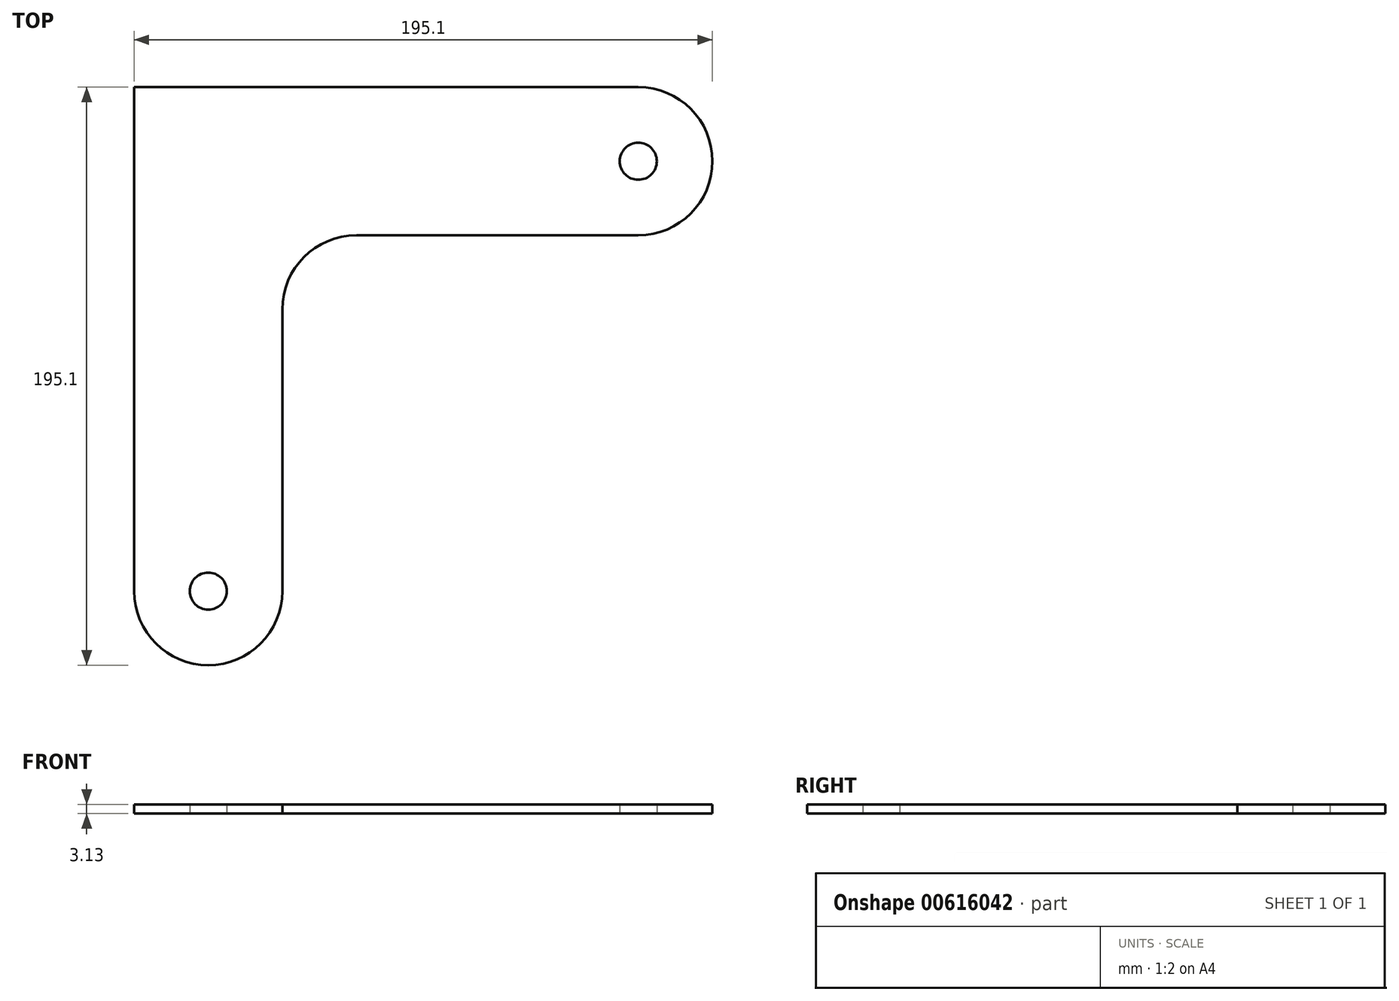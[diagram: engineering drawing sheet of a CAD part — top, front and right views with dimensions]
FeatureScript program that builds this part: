
annotation { "Feature Type Name" : "Feature", "Feature Type Description" : "" }
export const myFeature = defineFeature(function(context is Context, id is Id, definition is map)
    precondition{}
    {
        {
            var Q0;
            Q0=qCreatedBy(makeId("Top.planeOp"),FACE);
            var sketch = newSketch(context, id + "F0", { "sketchPlane" : qUnion([Q0])});
            skLineSegment(sketch, "E0", {"start": v(170.1, 0) * mm, "end": v(0, 0) * mm});
            skLineSegment(sketch, "E1", {"start": v(0, 0) * mm, "end": v(0, -170.1) * mm});
            skLineSegment(sketch, "E2", {"start": v(50, -170.1) * mm, "end": v(50, -75) * mm});
            skLineSegment(sketch, "E3", {"start": v(75, -50) * mm, "end": v(170.1, -50) * mm});
            skArc(sketch, "E4", {"start": v(0, -170.1) * mm, "mid": v(25, -195.1) * mm, "end": v(50, -170.1) * mm});
            skArc(sketch, "E5", {"start": v(170.1, -50) * mm, "mid": v(195.1, -25) * mm, "end": v(170.1, 0) * mm});
            skCircle(sketch, "E6", {"center": v(170.1, -25) * mm, "radius": 6.25 * mm});
            skCircle(sketch, "E7", {"center": v(25, -170.1) * mm, "radius": 6.25 * mm});
            skPoint(sketch, "E8.visualSharp", {"position": v(50, -50) * mm});
            skArc(sketch, "E8.filletArc", {"start": v(75, -50) * mm, "mid": v(57.32, -57.32) * mm, "end": v(50, -75) * mm});
            skSolve(sketch);
        }
        {
            var Q0;
            Q0=makeQuery(id+"F0.imprint","IMPRINT",FACE,{"disambiguationData":[TD([[makeQuery(id+"F0.imprint","IMPRINT",EDGE,{"derivedFrom":sQuery(id+"F0.wireOp",EDGE,"E0")}),1.0]])]});
            extrude(context, id + "F1", {"entities" : qUnion([Q0]), "depth" : 3.12 * mm, "offsetDistance" : 25 * mm});
        }
    });
